# Revit family: Furniture_Other_Sjobergs_Workbench_Junior_4
name_source: partatom
category: Furniture
revit_build: Autodesk Revit 2017 (Build: 20160225_1515(x64)
units: mm (PartAtom-declared; Revit-internal decimal feet)

## family parameters
Always vertical = Yes
Cut with Voids When Loaded = No
OmniClass Number = 23.40.70.14
OmniClass Title = Retail and Commercial Equipment and Furnishings
Room Calculation Point = No
Shared = No
Work Plane-Based = No

## types (1)
- 33360 Sjobergs Bench Junior 4
    AssetType = Movable
    BIMObjectName = Furniture_Other_Sjobergs_Workbench_Junior_4
    Brand = Sjöbergs
    Category = Hobby
    Collection = Planer Benches
    Color = Wooden
    Constituents = 33360 Junior x 4
    ConvergoRefNr = 0184-2005-0020-SE
    Cost = 0 $
    Description = Intended for pre-school and recreational activities. JUNIOR-4 is delivered complete with trestle in wood and bench dogs.
    DurationUnit = Year
    Finish = Solid birch
    IfcExportAs = IfcFurnishingElementType
    IfcExportType = TABLE
    MainColor = Wooden
    Manufacturer = Sjöbergs
    ManufacturerName = Sjöbergs
    ManufacturerURL = https://www.sjobergs.se
    Material = Wood, metal
    Model = 33360 Sjobergs Bench Junior 4
    ModelReference = 33360
    NBSDescription = School art, design and technology tables and workbenches;
    NBSReference = 45-35-20/320
    Name = Sjobergs_Workbench_Junior_4
    NominalDepth = 1434 mm
    NominalHeight = 700 mm
    NominalLength = 1434 mm
    ProductDatasheet = https://www.sjobergs.se
    ProductInformation = Intended for pre-school and recreational activities. JUNIOR-4 is delivered complete with trestle in wood and bench dogs.
    Shape = Sculptured
    Size = 1300x1300x700 mm
    TableMainMaterial = Beech
    TableSecondaryMaterial = Black Metal
    URL = https://www.sjobergs.se
    Uniclass2 = Pr_40_50_21
    Uniclass2015Description = Desks, Tables And Worktops
    Uniclass2015Reference = Pr_40_50_21_76
    Version = 1
    VersionDate = 26/06/2020
    WarrantyDurationUnit = Year
    Weight = 55 kg

## geometry (parser evidence)
native form markers: Sweep x10
no freeform markers — native parametric forms only
